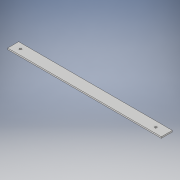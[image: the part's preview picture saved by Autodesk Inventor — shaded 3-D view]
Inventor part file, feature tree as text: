
AUTODESK INVENTOR PART (.ipt)
format: ipt  version: 2018.3 (Build 223284000, 284)  size: 105,472 bytes
history: native  units: in
note: dims shown in document units (in); Inventor stores cm internally (conversion verified against a paired STEP export)
features: extrude x2, sketch x2
ambient origin geometry x8: Origin, YZ Plane, XZ Plane, XY Plane, X Axis, Y Axis, Z Axis, Center Point
bodies: Solid1 (feature_tree)
feature tree (4):
  extrude  "Extrusion1"  Depth=1.0in
  extrude  "Extrusion2"  Depth=1.0in
  sketch  "Sketch1"  dims[d0=14.0in d1=1.0in]
  sketch  "Sketch2"  dims[d2=0.125in d3=0.0in d4=1.0in d5=12.335in d6=0.2031in d7=0.2031in d8=0.125in d9=0.0in]
